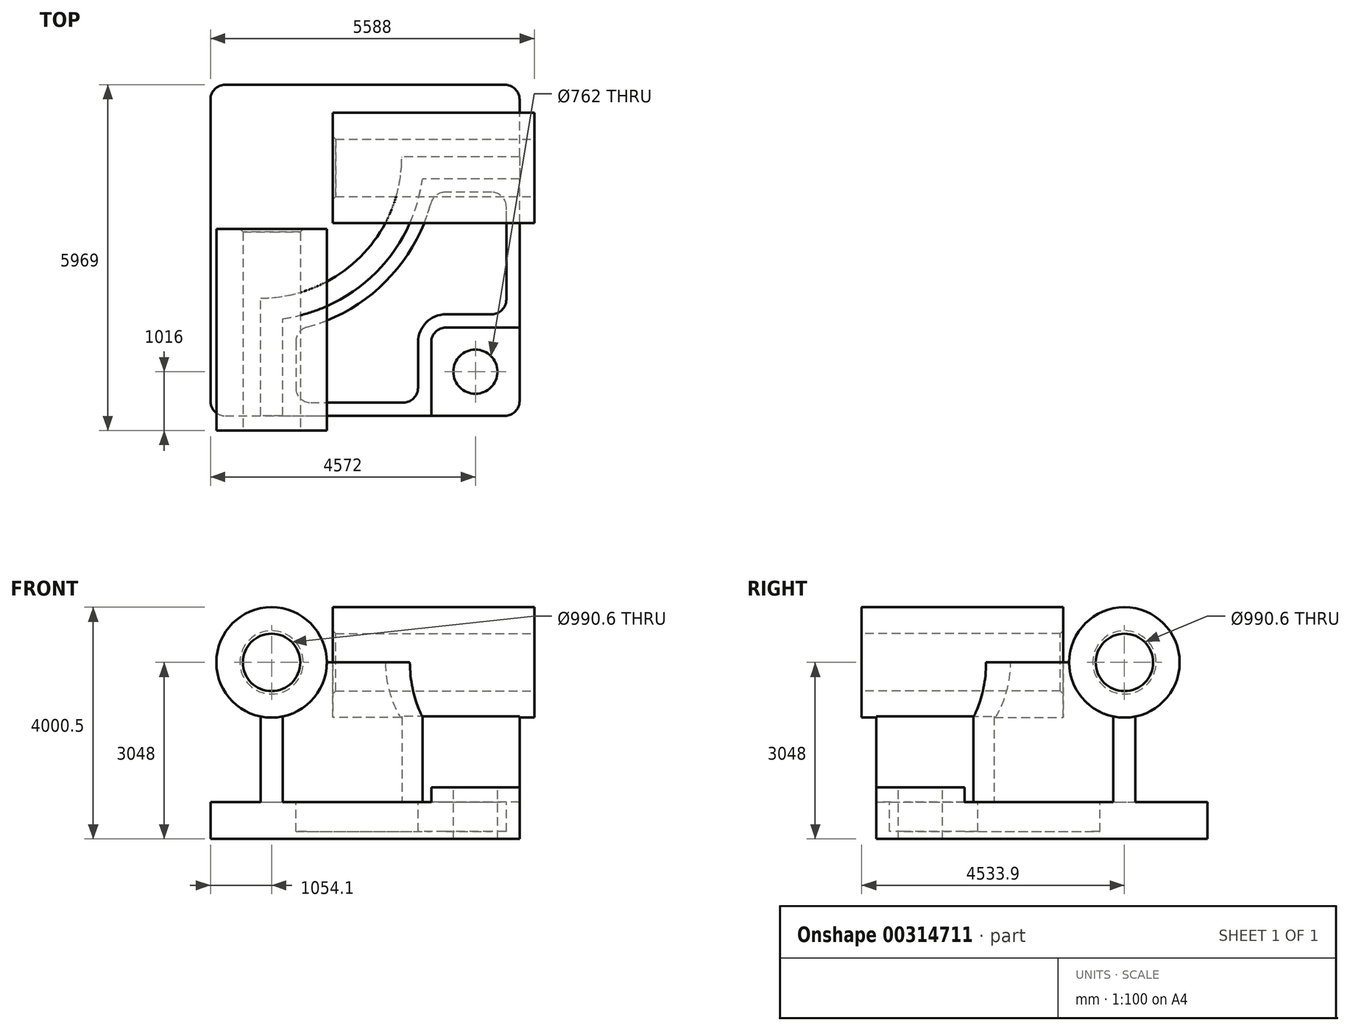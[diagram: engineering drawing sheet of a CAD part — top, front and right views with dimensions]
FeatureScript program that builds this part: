
annotation { "Feature Type Name" : "Feature", "Feature Type Description" : "" }
export const myFeature = defineFeature(function(context is Context, id is Id, definition is map)
    precondition{}
    {
        {
            var Q0;
            Q0=qCreatedBy(makeId("Top.planeOp"),FACE);
            var sketch = newSketch(context, id + "F0", { "sketchPlane" : qUnion([Q0])});
            skLineSegment(sketch, "E0.bottom", {"start": v(-2667, -2857.5) * mm, "end": v(2667, -2857.5) * mm});
            skLineSegment(sketch, "E0.top", {"start": v(-2667, 2857.5) * mm, "end": v(2667, 2857.5) * mm});
            skLineSegment(sketch, "E0.left", {"start": v(-2667, -2857.5) * mm, "end": v(-2667, 2857.5) * mm});
            skLineSegment(sketch, "E0.right", {"start": v(2667, -2857.5) * mm, "end": v(2667, 2857.5) * mm});
            skPoint(sketch, "E0.middle", {"position": v(0, 0) * mm});
            skSolve(sketch);
        }
        {
            var Q0;
            Q0=makeQuery(id+"F0.imprint","IMPRINT",FACE,{"disambiguationData":[TD([[makeQuery(id+"F0.imprint","IMPRINT",EDGE,{"derivedFrom":sQuery(id+"F0.wireOp",EDGE,"E0.bottom")}),1.0]])]});
            extrude(context, id + "F1", {"entities" : qUnion([Q0]), "depth" : 635 * mm});
        }
        {
            var Q0;
            Q0=makeQuery(id+"F1.opExtrude","CAP_FACE",FACE,{"disambiguationData":[OSD([sQuery(id+"F0.wireOp",EDGE,"E0.bottom"),sQuery(id+"F0.wireOp",EDGE,"E0.top"),sQuery(id+"F0.wireOp",EDGE,"E0.left"),sQuery(id+"F0.wireOp",EDGE,"E0.right")])],"isStart":false});
            var sketch = newSketch(context, id + "F2", { "sketchPlane" : qUnion([Q0])});
            skLineSegment(sketch, "E1", {"start": v(-1803.4, -2857.5) * mm, "end": v(-1803.4, -825.5) * mm});
            skLineSegment(sketch, "E2", {"start": v(2667, 1612.9) * mm, "end": v(635, 1612.9) * mm});
            skArc(sketch, "E3", {"start": v(-1803.4, -825.5) * mm, "mid": v(-79.2, -111.3) * mm, "end": v(635, 1612.9) * mm});
            skLineSegment(sketch, "E4", {"start": v(-1803.4, 1612.9) * mm, "end": v(635, 1612.9) * mm, "construction": true});
            skLineSegment(sketch, "E5", {"start": v(-1803.4, 1612.9) * mm, "end": v(-1803.4, -825.5) * mm, "construction": true});
            skLineSegment(sketch, "E6.0", {"start": v(-1422.4, -2857.5) * mm, "end": v(-1422.4, -1180.64) * mm});
            skArc(sketch, "E6.1", {"start": v(-1422.4, -1180.64) * mm, "mid": v(190.22, -380.72) * mm, "end": v(990.14, 1231.9) * mm});
            skLineSegment(sketch, "E6.2", {"start": v(2667, 1231.9) * mm, "end": v(990.14, 1231.9) * mm});
            skLineSegment(sketch, "E7.0", {"start": v(2667, -2857.5) * mm, "end": v(2667, 2857.5) * mm});
            skLineSegment(sketch, "E8.0", {"start": v(-2667, -2857.5) * mm, "end": v(2667, -2857.5) * mm});
            skSolve(sketch);
        }
        {
            var Q0;
            {var subQ2=sQuery(id+"F2.wireOp",EDGE,"E1");Q0=makeQuery(id+"F2.imprint","IMPRINT",FACE,{"disambiguationData":[TD([[makeQuery(id+"F2.imprint","IMPRINT",EDGE,{"derivedFrom":subQ2}),-1.0]])]});}
            extrude(context, id + "F3", {"entities" : qUnion([Q0]), "operationType" : NewBodyOperationType.ADD, "depth" : 2413 * mm});
        }
        {
            var Q0;
            Q0=makeQuery(id+"F3.boolean.opBoolean","MERGE",FACE,{"derivedFrom":[makeQuery(id+"F1.opExtrude","SWEPT_FACE",FACE,{"disambiguationData":[OSD([sQuery(id+"F0.wireOp",EDGE,"E0.bottom")])]}),makeQuery(id+"F3.opExtrude","SWEPT_FACE",FACE,{"disambiguationData":[OSD([sQuery(id+"F2.wireOp",EDGE,"E8.0")])]})]});
            var sketch = newSketch(context, id + "F4", { "sketchPlane" : qUnion([Q0])});
            skCircle(sketch, "E9", {"center": v(-1612.9, 3048) * mm, "radius": 952.5 * mm});
            skSolve(sketch);
        }
        {
            var Q0;
            Q0 = qSketchRegion(id + "F4", true);
            extrude(context, id + "F5", {"entities" : qUnion([Q0]), "operationType" : NewBodyOperationType.ADD, "depth" : 254 * mm, "hasSecondDirection" : true, "secondDirectionOppositeDirection" : true, "secondDirectionDepth" : 3225.8 * mm});
        }
        {
            var Q0;
            Q0=makeQuery(id+"F3.boolean.opBoolean","MERGE",FACE,{"derivedFrom":[makeQuery(id+"F1.opExtrude","SWEPT_FACE",FACE,{"disambiguationData":[OSD([sQuery(id+"F0.wireOp",EDGE,"E0.right")])]}),makeQuery(id+"F3.opExtrude","SWEPT_FACE",FACE,{"disambiguationData":[OSD([sQuery(id+"F2.wireOp",EDGE,"E7.0")])]})]});
            var sketch = newSketch(context, id + "F6", { "sketchPlane" : qUnion([Q0])});
            skCircle(sketch, "E10", {"center": v(1422.4, 3048) * mm, "radius": 952.5 * mm});
            skSolve(sketch);
        }
        {
            var Q0;
            Q0 = qSketchRegion(id + "F6", true);
            extrude(context, id + "F7", {"entities" : qUnion([Q0]), "operationType" : NewBodyOperationType.ADD, "depth" : 254 * mm, "hasSecondDirection" : true, "secondDirectionOppositeDirection" : true, "secondDirectionDepth" : 3225.8 * mm});
        }
        {
            var Q0;
            {var subQ0=sQuery(id+"F0.wireOp",EDGE,"E0.right");var subQ1=sQuery(id+"F0.wireOp",EDGE,"E0.bottom");Q0=makeQuery(id+"F3.boolean.opBoolean","SPLIT",FACE,{"disambiguationData":[TD([makeQuery(id+"F3.opExtrude","SWEPT_FACE",FACE,{"disambiguationData":[OSD([sQuery(id+"F2.wireOp",EDGE,"E6.0")])]})])],"derivedFrom":makeQuery(id+"F1.opExtrude","CAP_FACE",FACE,{"disambiguationData":[OSD([subQ1,sQuery(id+"F0.wireOp",EDGE,"E0.top"),sQuery(id+"F0.wireOp",EDGE,"E0.left"),subQ0])],"isStart":false})});}
            var sketch = newSketch(context, id + "F8", { "sketchPlane" : qUnion([Q0])});
            skLineSegment(sketch, "E11.bottom", {"start": v(2667, -2857.5) * mm, "end": v(1143, -2857.5) * mm});
            skLineSegment(sketch, "E11.top", {"start": v(2667, -1333.5) * mm, "end": v(1143, -1333.5) * mm});
            skLineSegment(sketch, "E11.left", {"start": v(2667, -2857.5) * mm, "end": v(2667, -1333.5) * mm});
            skLineSegment(sketch, "E11.right", {"start": v(1143, -2857.5) * mm, "end": v(1143, -1333.5) * mm});
            skSolve(sketch);
        }
        {
            var Q0;
            Q0=makeQuery(id+"F8.imprint","IMPRINT",FACE,{"disambiguationData":[TD([[makeQuery(id+"F8.imprint","IMPRINT",EDGE,{"derivedFrom":sQuery(id+"F8.wireOp",EDGE,"E11.bottom")}),1.0]])]});
            extrude(context, id + "F9", {"entities" : qUnion([Q0]), "operationType" : NewBodyOperationType.ADD, "depth" : 254 * mm});
        }
        {
            var Q0;
            Q0=makeQuery(id+"F9.opExtrude","SWEPT_EDGE",EDGE,{"disambiguationData":[OSD([sQuery(id+"F8.wireOp",EDGE,"E11.top"),sQuery(id+"F8.wireOp",EDGE,"E11.right")])]});
            fillet(context, id + "F10", {"entities" : qUnion([Q0]), "radius" : 254 * mm, "tangentPropagation" : true, "allowEdgeOverflow" : false});
        }
        {
            var Q0;
            {var subQ0=sQuery(id+"F0.wireOp",EDGE,"E0.right");var subQ1=sQuery(id+"F0.wireOp",EDGE,"E0.bottom");Q0=makeQuery(id+"F3.boolean.opBoolean","SPLIT",FACE,{"disambiguationData":[TD([makeQuery(id+"F3.opExtrude","SWEPT_FACE",FACE,{"disambiguationData":[OSD([sQuery(id+"F2.wireOp",EDGE,"E6.0")])]})])],"derivedFrom":makeQuery(id+"F1.opExtrude","CAP_FACE",FACE,{"disambiguationData":[OSD([subQ1,sQuery(id+"F0.wireOp",EDGE,"E0.top"),sQuery(id+"F0.wireOp",EDGE,"E0.left"),subQ0])],"isStart":false})});}
            var sketch = newSketch(context, id + "F11", { "sketchPlane" : qUnion([Q0])});
            skLineSegment(sketch, "E12.0", {"start": v(-1193.8, -1373.52) * mm, "end": v(-1193.8, -2628.9) * mm});
            skArc(sketch, "E12.1", {"start": v(1183.02, 1003.3) * mm, "mid": v(351.86, -542.36) * mm, "end": v(-1193.8, -1373.52) * mm});
            skLineSegment(sketch, "E12.2", {"start": v(-1193.8, -2628.9) * mm, "end": v(914.4, -2628.9) * mm});
            skLineSegment(sketch, "E12.3", {"start": v(2438.4, 1003.3) * mm, "end": v(1183.02, 1003.3) * mm});
            skLineSegment(sketch, "E12.4", {"start": v(914.4, -2628.9) * mm, "end": v(914.4, -1587.5) * mm});
            skArc(sketch, "E12.5", {"start": v(914.4, -1587.5) * mm, "mid": v(1055.75, -1246.25) * mm, "end": v(1397, -1104.9) * mm});
            skLineSegment(sketch, "E12.6", {"start": v(1397, -1104.9) * mm, "end": v(2438.4, -1104.9) * mm});
            skLineSegment(sketch, "E12.7", {"start": v(2438.4, -1104.9) * mm, "end": v(2438.4, 1003.3) * mm});
            skSolve(sketch);
        }
        {
            var Q0;
            Q0 = qSketchRegion(id + "F11", true);
            extrude(context, id + "F12", {"entities" : qUnion([Q0]), "operationType" : NewBodyOperationType.REMOVE, "oppositeDirection" : true, "depth" : 508 * mm});
        }
        {
            var Q0;
            Q0=makeQuery(id+"F9.opExtrude","CAP_FACE",FACE,{"disambiguationData":[OSD([sQuery(id+"F8.wireOp",EDGE,"E11.bottom"),sQuery(id+"F8.wireOp",EDGE,"E11.top"),sQuery(id+"F8.wireOp",EDGE,"E11.left"),sQuery(id+"F8.wireOp",EDGE,"E11.right")])],"isStart":false});
            var sketch = newSketch(context, id + "F13", { "sketchPlane" : qUnion([Q0])});
            skCircle(sketch, "E13", {"center": v(1905, -2095.5) * mm, "radius": 381 * mm});
            skSolve(sketch);
        }
        {
            var Q0;
            Q0=sQuery(id+"F13.wireOp",VERTEX,"E13.center");
            var Q1;
            Q1=makeQuery(id+"F1.opExtrude","SWEPT_BODY",BODY,{"disambiguationData":[OSD([sQuery(id+"F0.wireOp",EDGE,"E0.bottom"),sQuery(id+"F0.wireOp",EDGE,"E0.top"),sQuery(id+"F0.wireOp",EDGE,"E0.left"),sQuery(id+"F0.wireOp",EDGE,"E0.right")])]});
            hole(context, id + "F14", {"style" : HoleStyle.C_BORE, "endStyle" : HoleEndStyle.THROUGH, "holeDiameter" : 762 * mm, "cBoreDiameter" : 762 * mm, "cBoreDepth" : 254 * mm, "tappedDepth" : 12.7 * mm, "tapClearance" : 3, "locations" : qUnion([Q0]), "scope" : qUnion([Q1])});
        }
        {
            var Q0;
            Q0=makeQuery(id+"F12.boolean.opBoolean","COPY",EDGE,{"derivedFrom":makeQuery(id+"F12.opExtrude","SWEPT_EDGE",EDGE,{"disambiguationData":[OSD([sQuery(id+"F11.wireOp",EDGE,"E12.0"),sQuery(id+"F11.wireOp",EDGE,"E12.1")])]})});
            var Q1;
            Q1=makeQuery(id+"F12.boolean.opBoolean","COPY",EDGE,{"derivedFrom":makeQuery(id+"F12.opExtrude","SWEPT_EDGE",EDGE,{"disambiguationData":[OSD([sQuery(id+"F11.wireOp",EDGE,"E12.1"),sQuery(id+"F11.wireOp",EDGE,"E12.3")])]})});
            var Q2;
            Q2=makeQuery(id+"F12.boolean.opBoolean","COPY",EDGE,{"derivedFrom":makeQuery(id+"F12.opExtrude","SWEPT_EDGE",EDGE,{"disambiguationData":[OSD([sQuery(id+"F11.wireOp",EDGE,"E12.0"),sQuery(id+"F11.wireOp",EDGE,"E12.2")])]})});
            var Q3;
            Q3=makeQuery(id+"F12.boolean.opBoolean","COPY",EDGE,{"derivedFrom":makeQuery(id+"F12.opExtrude","SWEPT_EDGE",EDGE,{"disambiguationData":[OSD([sQuery(id+"F11.wireOp",EDGE,"E12.6"),sQuery(id+"F11.wireOp",EDGE,"E12.7")])]})});
            var Q4;
            Q4=makeQuery(id+"F12.boolean.opBoolean","COPY",EDGE,{"derivedFrom":makeQuery(id+"F12.opExtrude","SWEPT_EDGE",EDGE,{"disambiguationData":[OSD([sQuery(id+"F11.wireOp",EDGE,"E12.2"),sQuery(id+"F11.wireOp",EDGE,"E12.4")])]})});
            fillet(context, id + "F15", {"entities" : qUnion([Q0, Q1, Q2, Q3, Q4]), "radius" : 254 * mm, "tangentPropagation" : true, "allowEdgeOverflow" : false});
        }
        {
            var Q0;
            Q0=makeQuery(id+"F12.boolean.opBoolean","COPY",EDGE,{"derivedFrom":makeQuery(id+"F12.opExtrude","SWEPT_EDGE",EDGE,{"disambiguationData":[OSD([sQuery(id+"F11.wireOp",EDGE,"E12.3"),sQuery(id+"F11.wireOp",EDGE,"E12.7")])]})});
            fillet(context, id + "F16", {"entities" : qUnion([Q0]), "radius" : 254 * mm, "tangentPropagation" : true, "allowEdgeOverflow" : false});
        }
        {
            var Q0;
            Q0=makeQuery(id+"F5.opExtrude","CAP_FACE",FACE,{"disambiguationData":[OSD([sQuery(id+"F4.wireOp",EDGE,"E9")])],"isStart":false});
            var sketch = newSketch(context, id + "F17", { "sketchPlane" : qUnion([Q0])});
            skCircle(sketch, "E14", {"center": v(-1612.9, 3048) * mm, "radius": 495.3 * mm});
            skSolve(sketch);
        }
        {
            var Q0;
            Q0=makeQuery(id+"F17.imprint","IMPRINT",FACE,{"disambiguationData":[TD([[makeQuery(id+"F17.imprint","IMPRINT",EDGE,{"derivedFrom":sQuery(id+"F17.wireOp",EDGE,"E14")}),1.0]])]});
            extrude(context, id + "F18", {"entities" : qUnion([Q0]), "operationType" : NewBodyOperationType.REMOVE, "endBound" : BoundingType.THROUGH_ALL, "oppositeDirection" : true, "depth" : 25.4 * mm});
        }
        {
            var Q0;
            Q0=makeQuery(id+"F7.opExtrude","CAP_FACE",FACE,{"disambiguationData":[OSD([sQuery(id+"F6.wireOp",EDGE,"E10")])],"isStart":false});
            var sketch = newSketch(context, id + "F19", { "sketchPlane" : qUnion([Q0])});
            skCircle(sketch, "E15", {"center": v(1422.4, 3048) * mm, "radius": 495.3 * mm});
            skSolve(sketch);
        }
        {
            var Q0;
            Q0=makeQuery(id+"F19.imprint","IMPRINT",FACE,{"disambiguationData":[TD([[makeQuery(id+"F19.imprint","IMPRINT",EDGE,{"derivedFrom":sQuery(id+"F19.wireOp",EDGE,"E15")}),1.0]])]});
            extrude(context, id + "F20", {"entities" : qUnion([Q0]), "operationType" : NewBodyOperationType.REMOVE, "endBound" : BoundingType.THROUGH_ALL, "oppositeDirection" : true, "depth" : 25.4 * mm});
        }
        {
            var Q0;
            Q0=makeQuery(id+"F18.boolean.opBoolean","COPY",EDGE,{"derivedFrom":makeQuery(id+"F18.opExtrude","CAP_EDGE",EDGE,{"disambiguationData":[OSD([sQuery(id+"F17.wireOp",EDGE,"E14")])],"isStart":true})});
            var Q1;
            Q1=makeQuery(id+"F20.boolean.opBoolean","COPY",EDGE,{"derivedFrom":makeQuery(id+"F20.opExtrude","CAP_EDGE",EDGE,{"disambiguationData":[OSD([sQuery(id+"F19.wireOp",EDGE,"E15")])],"isStart":true})});
            var Q2;
            Q2=makeQuery(id+"F18.boolean.opBoolean","INTERSECT",EDGE,{"derivedFrom":[makeQuery(id+"F5.opExtrude","CAP_FACE",FACE,{"disambiguationData":[OSD([sQuery(id+"F4.wireOp",EDGE,"E9")])],"isStart":true}),makeQuery(id+"F18.opExtrude","SWEPT_FACE",FACE,{"disambiguationData":[OSD([sQuery(id+"F17.wireOp",EDGE,"E14")])]})]});
            var Q3;
            Q3=makeQuery(id+"F20.boolean.opBoolean","INTERSECT",EDGE,{"derivedFrom":[makeQuery(id+"F7.opExtrude","CAP_FACE",FACE,{"disambiguationData":[OSD([sQuery(id+"F6.wireOp",EDGE,"E10")])],"isStart":true}),makeQuery(id+"F20.opExtrude","SWEPT_FACE",FACE,{"disambiguationData":[OSD([sQuery(id+"F19.wireOp",EDGE,"E15")])]})]});
            chamfer(context, id + "F21", {"entities" : qUnion([Q0, Q1, Q2, Q3]), "width" : 50.8 * mm, "tangentPropagation" : true});
        }
        {
            var Q0;
            Q0=makeQuery(id+"F1.opExtrude","SWEPT_EDGE",EDGE,{"disambiguationData":[OSD([sQuery(id+"F0.wireOp",EDGE,"E0.bottom"),sQuery(id+"F0.wireOp",EDGE,"E0.left")])]});
            var Q1;
            Q1=makeQuery(id+"F9.boolean.opBoolean","MERGE",EDGE,{"derivedFrom":[makeQuery(id+"F1.opExtrude","SWEPT_EDGE",EDGE,{"disambiguationData":[OSD([sQuery(id+"F0.wireOp",EDGE,"E0.bottom"),sQuery(id+"F0.wireOp",EDGE,"E0.right")])]}),makeQuery(id+"F9.opExtrude","SWEPT_EDGE",EDGE,{"disambiguationData":[OSD([sQuery(id+"F8.wireOp",EDGE,"E11.bottom"),sQuery(id+"F8.wireOp",EDGE,"E11.left")])]})]});
            var Q2;
            Q2=makeQuery(id+"F1.opExtrude","SWEPT_EDGE",EDGE,{"disambiguationData":[OSD([sQuery(id+"F0.wireOp",EDGE,"E0.top"),sQuery(id+"F0.wireOp",EDGE,"E0.right")])]});
            var Q3;
            Q3=makeQuery(id+"F1.opExtrude","SWEPT_EDGE",EDGE,{"disambiguationData":[OSD([sQuery(id+"F0.wireOp",EDGE,"E0.top"),sQuery(id+"F0.wireOp",EDGE,"E0.left")])]});
            fillet(context, id + "F22", {"entities" : qUnion([Q0, Q1, Q2, Q3]), "radius" : 254 * mm, "tangentPropagation" : true, "allowEdgeOverflow" : false});
        }
    });
